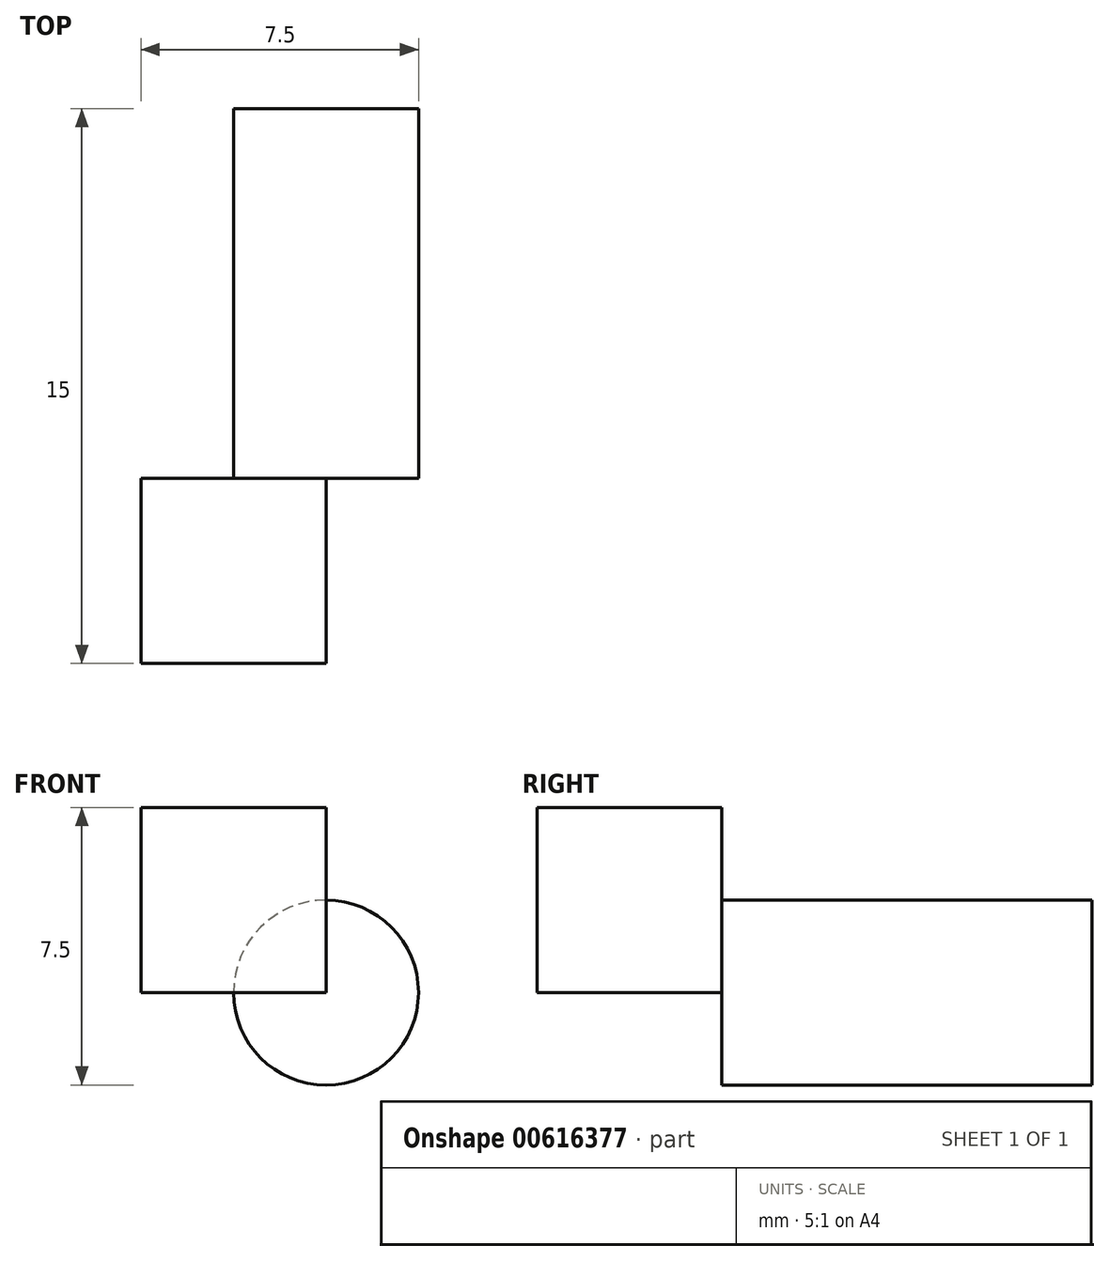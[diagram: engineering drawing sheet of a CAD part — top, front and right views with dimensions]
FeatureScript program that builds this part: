
annotation { "Feature Type Name" : "Feature", "Feature Type Description" : "" }
export const myFeature = defineFeature(function(context is Context, id is Id, definition is map)
    precondition{}
    {
        {
            var Q0;
            Q0=qCreatedBy(makeId("Front.planeOp"),FACE);
            var sketch = newSketch(context, id + "F0", { "sketchPlane" : qUnion([Q0])});
            skCircle(sketch, "E0", {"center": v(0, 0) * mm, "radius": 2.5 * mm});
            skSolve(sketch);
        }
        {
            var Q0;
            Q0 = qSketchRegion(id + "F0", true);
            extrude(context, id + "F1", {"entities" : qUnion([Q0]), "depth" : 10 * mm, "offsetDistance" : 25 * mm});
        }
        {
            var Q0;
            Q0=makeQuery(id+"F1.opExtrude","CAP_FACE",FACE,{"disambiguationData":[OSD([sQuery(id+"F0.wireOp",EDGE,"E0")])],"isStart":false});
            var sketch = newSketch(context, id + "F2", { "sketchPlane" : qUnion([Q0])});
            skLineSegment(sketch, "E1.bottom", {"start": v(-5, 5) * mm, "end": v(5, 5) * mm});
            skLineSegment(sketch, "E1.top", {"start": v(-5, -5) * mm, "end": v(5, -5) * mm});
            skLineSegment(sketch, "E1.left", {"start": v(-5, 5) * mm, "end": v(-5, -5) * mm});
            skLineSegment(sketch, "E1.right", {"start": v(5, 5) * mm, "end": v(5, -5) * mm});
            skPoint(sketch, "E1.middle", {"position": v(0, 0) * mm});
            skSolve(sketch);
        }
        {
            var Q0;
            Q0 = qSketchRegion(id + "F2", true);
            extrude(context, id + "F3", {"entities" : qUnion([Q0]), "operationType" : NewBodyOperationType.ADD, "depth" : 5 * mm, "offsetDistance" : 25 * mm});
        }
        {
            var Q0;
            Q0=makeQuery(id+"F3.opExtrude","CAP_FACE",FACE,{"disambiguationData":[OSD([sQuery(id+"F2.wireOp",EDGE,"E1.bottom"),sQuery(id+"F2.wireOp",EDGE,"E1.top"),sQuery(id+"F2.wireOp",EDGE,"E1.left"),sQuery(id+"F2.wireOp",EDGE,"E1.right")])],"isStart":false});
            var sketch = newSketch(context, id + "F4", { "sketchPlane" : qUnion([Q0])});
            skLineSegment(sketch, "E2.bottom", {"start": v(0, 0) * mm, "end": v(-5, 0) * mm});
            skLineSegment(sketch, "E2.top", {"start": v(5, -5) * mm, "end": v(-5, -5) * mm});
            skLineSegment(sketch, "E2.left", {"start": v(5, 0) * mm, "end": v(5, -5) * mm});
            skLineSegment(sketch, "E2.right", {"start": v(-5, 0) * mm, "end": v(-5, -5) * mm});
            skLineSegment(sketch, "E3.top", {"start": v(0, 5) * mm, "end": v(5, 5) * mm});
            skLineSegment(sketch, "E3.left", {"start": v(0, 0) * mm, "end": v(0, 5) * mm});
            skLineSegment(sketch, "E3.right", {"start": v(5, 0) * mm, "end": v(5, 5) * mm});
            skSolve(sketch);
        }
        {
            var Q0;
            Q0 = qSketchRegion(id + "F4", true);
            var Q1;
            Q1=makeQuery(id+"F3.opExtrude","CAP_FACE",FACE,{"disambiguationData":[OSD([sQuery(id+"F2.wireOp",EDGE,"E1.bottom"),sQuery(id+"F2.wireOp",EDGE,"E1.top"),sQuery(id+"F2.wireOp",EDGE,"E1.left"),sQuery(id+"F2.wireOp",EDGE,"E1.right")])],"isStart":true});
            extrude(context, id + "F5", {"entities" : qUnion([Q0]), "operationType" : NewBodyOperationType.REMOVE, "endBound" : BoundingType.UP_TO_SURFACE, "oppositeDirection" : true, "depth" : 25 * mm, "endBoundEntityFace" : qUnion([Q1]), "offsetDistance" : 25 * mm});
        }
    });
